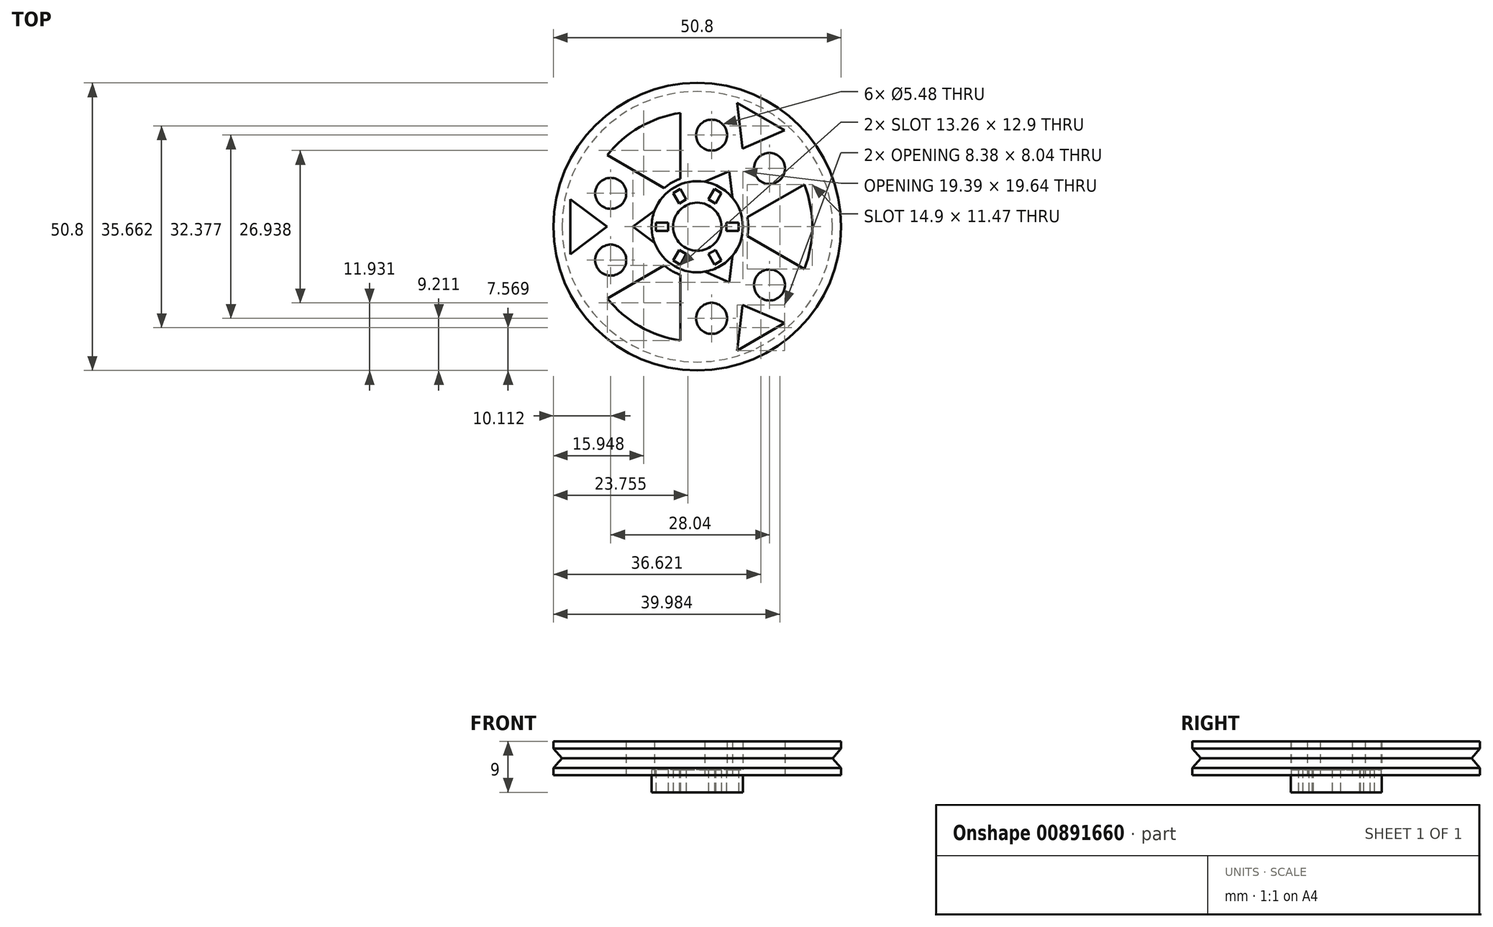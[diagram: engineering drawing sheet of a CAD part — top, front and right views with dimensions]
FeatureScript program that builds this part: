
annotation { "Feature Type Name" : "Feature", "Feature Type Description" : "" }
export const myFeature = defineFeature(function(context is Context, id is Id, definition is map)
    precondition{}
    {
        {
            var Q0;
            Q0=qCreatedBy(makeId("Top.planeOp"),FACE);
            var sketch = newSketch(context, id + "F0", { "sketchPlane" : qUnion([Q0])});
            skCircle(sketch, "E0", {"center": v(0, 0) * mm, "radius": 25.4 * mm});
            skCircle(sketch, "E1", {"center": v(0, 0) * mm, "radius": 8.05 * mm});
            skArc(sketch, "E2", {"start": v(-3, 8.49) * mm, "mid": v(-4.5, 7.8) * mm, "end": v(-5.85, 6.84) * mm});
            skArc(sketch, "E3.0", {"start": v(-3, 20.1) * mm, "mid": v(-10.16, 17.6) * mm, "end": v(-15.9, 12.65) * mm});
            skPoint(sketch, "E4.orphan", {"position": v(0, 21.15) * mm});
            skLineSegment(sketch, "E5.0", {"start": v(-3, 8.49) * mm, "end": v(-3, 20.1) * mm});
            skLineSegment(sketch, "E6.0", {"start": v(8.85, 1.64) * mm, "end": v(18.9, 7.45) * mm});
            skPoint(sketch, "E7.start.orphan", {"position": v(0, 8.05) * mm});
            skLineSegment(sketch, "E8.1.0", {"start": v(-5.85, -6.84) * mm, "end": v(-15.9, -12.65) * mm});
            skLineSegment(sketch, "E8.1.1", {"start": v(-5.85, 6.84) * mm, "end": v(-15.9, 12.65) * mm});
            skArc(sketch, "E9.trimOffspring", {"start": v(8.85, -1.64) * mm, "mid": v(9, 0) * mm, "end": v(8.85, 1.64) * mm});
            skArc(sketch, "E10.trimOffspring", {"start": v(18.9, -7.45) * mm, "mid": v(20.32, 0) * mm, "end": v(18.9, 7.45) * mm});
            skLineSegment(sketch, "E11.1.2.0", {"start": v(8.85, -1.64) * mm, "end": v(18.9, -7.45) * mm});
            skLineSegment(sketch, "E11.3.2.0", {"start": v(-3, -8.49) * mm, "end": v(-3, -20.1) * mm});
            skArc(sketch, "E12.trimOffspring", {"start": v(-15.9, -12.65) * mm, "mid": v(-10.16, -17.6) * mm, "end": v(-3, -20.1) * mm});
            skArc(sketch, "E13.trimOffspring", {"start": v(-5.85, -6.84) * mm, "mid": v(-4.5, -7.8) * mm, "end": v(-3, -8.49) * mm});
            skLineSegment(sketch, "E14", {"start": v(-22.44, 0) * mm, "end": v(-15.95, 0) * mm});
            skLineSegment(sketch, "E15", {"start": v(-15.95, 0) * mm, "end": v(-22.44, -4.84) * mm});
            skLineSegment(sketch, "E16", {"start": v(-22.44, -4.84) * mm, "end": v(-22.44, 0) * mm});
            skLineSegment(sketch, "E17.MirrorCS", {"start": v(-15.95, 0) * mm, "end": v(-22.44, 4.84) * mm});
            skLineSegment(sketch, "E18.MirrorCS", {"start": v(-22.44, 4.84) * mm, "end": v(-22.44, 0) * mm});
            skCircle(sketch, "E19", {"center": v(-15.29, -5.9) * mm, "radius": 2.74 * mm});
            skCircle(sketch, "E20.MirrorC", {"center": v(-15.29, 5.9) * mm, "radius": 2.74 * mm});
            skLineSegment(sketch, "E21", {"start": v(-13.64, -0.96) * mm, "end": v(-13.64, 1.42) * mm, "construction": true});
            skLineSegment(sketch, "E22.MirrorCS", {"start": v(-11.34, 0) * mm, "end": v(-4.84, 4.84) * mm});
            skLineSegment(sketch, "E23.MirrorCS", {"start": v(-11.34, 0) * mm, "end": v(-4.84, -4.84) * mm});
            skLineSegment(sketch, "E24.MirrorCS", {"start": v(-4.84, -4.84) * mm, "end": v(-4.84, 0) * mm});
            skLineSegment(sketch, "E25.MirrorCS", {"start": v(-4.84, 4.84) * mm, "end": v(-4.84, 0) * mm});
            skLineSegment(sketch, "E26.1.0", {"start": v(7.97, -13.8) * mm, "end": v(7.03, -21.85) * mm});
            skLineSegment(sketch, "E26.1.1", {"start": v(7.97, -13.8) * mm, "end": v(15.4, -17.02) * mm});
            skLineSegment(sketch, "E26.1.2", {"start": v(15.4, -17.02) * mm, "end": v(11.22, -19.44) * mm});
            skLineSegment(sketch, "E26.1.3", {"start": v(7.03, -21.85) * mm, "end": v(11.22, -19.44) * mm});
            skCircle(sketch, "E26.1.4", {"center": v(2.54, -16.19) * mm, "radius": 2.74 * mm});
            skCircle(sketch, "E26.1.5", {"center": v(12.75, -10.3) * mm, "radius": 2.74 * mm});
            skLineSegment(sketch, "E26.1.6", {"start": v(5.67, -9.82) * mm, "end": v(-1.77, -6.61) * mm});
            skLineSegment(sketch, "E26.1.7", {"start": v(-1.77, -6.61) * mm, "end": v(2.42, -4.2) * mm});
            skLineSegment(sketch, "E26.1.8", {"start": v(6.61, -1.78) * mm, "end": v(2.42, -4.2) * mm});
            skLineSegment(sketch, "E26.1.9", {"start": v(5.67, -9.82) * mm, "end": v(6.61, -1.78) * mm});
            skLineSegment(sketch, "E26.2.0", {"start": v(7.97, 13.8) * mm, "end": v(15.4, 17.02) * mm});
            skLineSegment(sketch, "E26.2.1", {"start": v(7.97, 13.8) * mm, "end": v(7.03, 21.85) * mm});
            skLineSegment(sketch, "E26.2.2", {"start": v(7.03, 21.85) * mm, "end": v(11.22, 19.44) * mm});
            skLineSegment(sketch, "E26.2.3", {"start": v(15.4, 17.02) * mm, "end": v(11.22, 19.44) * mm});
            skCircle(sketch, "E26.2.4", {"center": v(12.75, 10.3) * mm, "radius": 2.74 * mm});
            skCircle(sketch, "E26.2.5", {"center": v(2.54, 16.19) * mm, "radius": 2.74 * mm});
            skLineSegment(sketch, "E26.2.6", {"start": v(5.67, 9.82) * mm, "end": v(6.61, 1.78) * mm});
            skLineSegment(sketch, "E26.2.7", {"start": v(6.61, 1.78) * mm, "end": v(2.42, 4.2) * mm});
            skLineSegment(sketch, "E26.2.8", {"start": v(-1.77, 6.61) * mm, "end": v(2.42, 4.2) * mm});
            skLineSegment(sketch, "E26.2.9", {"start": v(5.67, 9.82) * mm, "end": v(-1.77, 6.61) * mm});
            skSolve(sketch);
        }
        {
            var Q0;
            Q0=makeQuery(id+"F0.imprint","IMPRINT",FACE,{"disambiguationData":[TD([[makeQuery(id+"F0.imprint","IMPRINT",EDGE,{"derivedFrom":sQuery(id+"F0.wireOp",EDGE,"E0")}),1.0]])]});
            var Q1;
            Q1=makeQuery(id+"F0.imprint","IMPRINT",FACE,{"disambiguationData":[TD([[makeQuery(id+"F0.imprint","IMPRINT",EDGE,{"derivedFrom":sQuery(id+"F0.wireOp",EDGE,"E1")}),-1.0]])]});
            extrude(context, id + "F1", {"entities" : qUnion([Q0, Q1]), "endBound" : BoundingType.SYMMETRIC, "depth" : 6 * mm, "offsetDistance" : 25.4 * mm});
        }
        {
            var Q0;
            Q0=makeQuery(id+"F1.opExtrude","CAP_FACE",FACE,{"disambiguationData":[OSD([sQuery(id+"F0.wireOp",EDGE,"E0"),sQuery(id+"F0.wireOp",EDGE,"E1"),sQuery(id+"F0.wireOp",EDGE,"E2"),sQuery(id+"F0.wireOp",EDGE,"E3.0"),sQuery(id+"F0.wireOp",EDGE,"E5.0"),sQuery(id+"F0.wireOp",EDGE,"E6.0"),sQuery(id+"F0.wireOp",EDGE,"E8.1.0"),sQuery(id+"F0.wireOp",EDGE,"E8.1.1"),sQuery(id+"F0.wireOp",EDGE,"E9.trimOffspring"),sQuery(id+"F0.wireOp",EDGE,"E10.trimOffspring"),sQuery(id+"F0.wireOp",EDGE,"E11.1.2.0"),sQuery(id+"F0.wireOp",EDGE,"E11.3.2.0"),sQuery(id+"F0.wireOp",EDGE,"E12.trimOffspring"),sQuery(id+"F0.wireOp",EDGE,"E13.trimOffspring"),sQuery(id+"F0.wireOp",EDGE,"E15"),sQuery(id+"F0.wireOp",EDGE,"E16"),sQuery(id+"F0.wireOp",EDGE,"E17.MirrorCS"),sQuery(id+"F0.wireOp",EDGE,"E18.MirrorCS"),sQuery(id+"F0.wireOp",EDGE,"E19"),sQuery(id+"F0.wireOp",EDGE,"E20.MirrorC"),sQuery(id+"F0.wireOp",EDGE,"E22.MirrorCS"),sQuery(id+"F0.wireOp",EDGE,"E23.MirrorCS"),sQuery(id+"F0.wireOp",EDGE,"E26.1.0"),sQuery(id+"F0.wireOp",EDGE,"E26.1.1"),sQuery(id+"F0.wireOp",EDGE,"E26.1.2"),sQuery(id+"F0.wireOp",EDGE,"E26.1.3"),sQuery(id+"F0.wireOp",EDGE,"E26.1.4"),sQuery(id+"F0.wireOp",EDGE,"E26.1.5"),sQuery(id+"F0.wireOp",EDGE,"E26.1.6"),sQuery(id+"F0.wireOp",EDGE,"E26.1.9"),sQuery(id+"F0.wireOp",EDGE,"E26.2.0"),sQuery(id+"F0.wireOp",EDGE,"E26.2.1"),sQuery(id+"F0.wireOp",EDGE,"E26.2.2"),sQuery(id+"F0.wireOp",EDGE,"E26.2.3"),sQuery(id+"F0.wireOp",EDGE,"E26.2.4"),sQuery(id+"F0.wireOp",EDGE,"E26.2.5"),sQuery(id+"F0.wireOp",EDGE,"E26.2.6"),sQuery(id+"F0.wireOp",EDGE,"E26.2.9")])],"isStart":true});
            var sketch = newSketch(context, id + "F2", { "sketchPlane" : qUnion([Q0])});
            skCircle(sketch, "E27", {"center": v(0, 0) * mm, "radius": 8.05 * mm});
            skCircle(sketch, "E28", {"center": v(0, 0) * mm, "radius": 4.25 * mm});
            skLineSegment(sketch, "E29.bottom", {"start": v(-5.15, 0.73) * mm, "end": v(-7.29, 0.73) * mm});
            skLineSegment(sketch, "E29.top", {"start": v(-5.15, -0.73) * mm, "end": v(-7.29, -0.73) * mm});
            skLineSegment(sketch, "E29.left", {"start": v(-5.15, 0.73) * mm, "end": v(-5.15, -0.73) * mm});
            skLineSegment(sketch, "E29.right", {"start": v(-7.29, 0.73) * mm, "end": v(-7.29, -0.73) * mm});
            skPoint(sketch, "E29.middle", {"position": v(-6.22, 0) * mm});
            skLineSegment(sketch, "E30.1.0", {"start": v(-3.2, -4.1) * mm, "end": v(-1.94, -4.83) * mm});
            skLineSegment(sketch, "E30.1.1", {"start": v(-3.2, -4.1) * mm, "end": v(-4.28, -5.95) * mm});
            skLineSegment(sketch, "E30.1.2", {"start": v(-4.28, -5.95) * mm, "end": v(-3.01, -6.68) * mm});
            skLineSegment(sketch, "E30.1.3", {"start": v(-1.94, -4.83) * mm, "end": v(-3.01, -6.68) * mm});
            skLineSegment(sketch, "E30.2.0", {"start": v(1.94, -4.83) * mm, "end": v(3.2, -4.1) * mm});
            skLineSegment(sketch, "E30.2.1", {"start": v(1.94, -4.83) * mm, "end": v(3.01, -6.68) * mm});
            skLineSegment(sketch, "E30.2.2", {"start": v(3.01, -6.68) * mm, "end": v(4.28, -5.95) * mm});
            skLineSegment(sketch, "E30.2.3", {"start": v(3.2, -4.1) * mm, "end": v(4.28, -5.95) * mm});
            skLineSegment(sketch, "E31.2.3.0", {"start": v(5.15, -0.73) * mm, "end": v(5.15, 0.73) * mm});
            skLineSegment(sketch, "E31.3.3.0", {"start": v(5.15, -0.73) * mm, "end": v(7.29, -0.73) * mm});
            skLineSegment(sketch, "E31.6.3.0", {"start": v(7.29, -0.73) * mm, "end": v(7.29, 0.73) * mm});
            skLineSegment(sketch, "E31.9.3.0", {"start": v(5.15, 0.73) * mm, "end": v(7.29, 0.73) * mm});
            skLineSegment(sketch, "E31.2.4.0", {"start": v(3.2, 4.1) * mm, "end": v(1.94, 4.83) * mm});
            skLineSegment(sketch, "E31.3.4.0", {"start": v(3.2, 4.1) * mm, "end": v(4.28, 5.95) * mm});
            skLineSegment(sketch, "E31.6.4.0", {"start": v(4.28, 5.95) * mm, "end": v(3.01, 6.68) * mm});
            skLineSegment(sketch, "E31.9.4.0", {"start": v(1.94, 4.83) * mm, "end": v(3.01, 6.68) * mm});
            skLineSegment(sketch, "E32.2.5.0", {"start": v(-1.94, 4.83) * mm, "end": v(-3.2, 4.1) * mm});
            skLineSegment(sketch, "E32.3.5.0", {"start": v(-1.94, 4.83) * mm, "end": v(-3.01, 6.68) * mm});
            skLineSegment(sketch, "E32.6.5.0", {"start": v(-3.01, 6.68) * mm, "end": v(-4.28, 5.95) * mm});
            skLineSegment(sketch, "E32.9.5.0", {"start": v(-3.2, 4.1) * mm, "end": v(-4.28, 5.95) * mm});
            skSolve(sketch);
        }
        {
            var Q0;
            Q0=makeQuery(id+"F2.imprint","IMPRINT",FACE,{"disambiguationData":[TD([[makeQuery(id+"F2.imprint","IMPRINT",EDGE,{"derivedFrom":sQuery(id+"F2.wireOp",EDGE,"E28")}),-1.0]])]});
            extrude(context, id + "F3", {"entities" : qUnion([Q0]), "operationType" : NewBodyOperationType.ADD, "oppositeDirection" : true, "depth" : 1 * mm, "offsetDistance" : 25.4 * mm});
        }
        {
            var Q0;
            Q0=qCreatedBy(makeId("Right.planeOp"),FACE);
            var sketch = newSketch(context, id + "F4", { "sketchPlane" : qUnion([Q0])});
            skLineSegment(sketch, "E33", {"start": v(25.4, 0) * mm, "end": v(23.9, 0) * mm});
            skLineSegment(sketch, "E34", {"start": v(23.9, 0) * mm, "end": v(25.42, -1.75) * mm});
            skLineSegment(sketch, "E35", {"start": v(25.42, -1.75) * mm, "end": v(25.4, 0) * mm});
            skLineSegment(sketch, "E36.MirrorCS", {"start": v(23.9, 0) * mm, "end": v(25.42, 1.75) * mm});
            skLineSegment(sketch, "E37.MirrorCS", {"start": v(25.42, 1.75) * mm, "end": v(25.4, 0) * mm});
            skLineSegment(sketch, "E38", {"start": v(0, 0) * mm, "end": v(0, 14.16) * mm, "construction": true});
            skSolve(sketch);
        }
        {
            var Q0;
            Q0 = qSketchRegion(id + "F4", true);
            var Q1;
            Q1=sQuery(id+"F4.wireOp",EDGE,"E38");
            revolve(context, id + "F5", {"operationType" : NewBodyOperationType.REMOVE, "surfaceOperationType" : NewSurfaceOperationType.NEW, "entities" : qUnion([Q0]), "axis" : qUnion([Q1]), "revolveType" : RevolveType.FULL, "oppositeDirection" : true});
        }
        {
            var Q0;
            Q0=makeQuery(id+"F3.boolean.opBoolean","MERGE",FACE,{"derivedFrom":[makeQuery(id+"F1.opExtrude","CAP_FACE",FACE,{"disambiguationData":[OSD([sQuery(id+"F0.wireOp",EDGE,"E0"),sQuery(id+"F0.wireOp",EDGE,"E1"),sQuery(id+"F0.wireOp",EDGE,"E2"),sQuery(id+"F0.wireOp",EDGE,"E3.0"),sQuery(id+"F0.wireOp",EDGE,"E5.0"),sQuery(id+"F0.wireOp",EDGE,"E6.0"),sQuery(id+"F0.wireOp",EDGE,"E8.1.0"),sQuery(id+"F0.wireOp",EDGE,"E8.1.1"),sQuery(id+"F0.wireOp",EDGE,"E9.trimOffspring"),sQuery(id+"F0.wireOp",EDGE,"E10.trimOffspring"),sQuery(id+"F0.wireOp",EDGE,"E11.1.2.0"),sQuery(id+"F0.wireOp",EDGE,"E11.3.2.0"),sQuery(id+"F0.wireOp",EDGE,"E12.trimOffspring"),sQuery(id+"F0.wireOp",EDGE,"E13.trimOffspring"),sQuery(id+"F0.wireOp",EDGE,"E15"),sQuery(id+"F0.wireOp",EDGE,"E16"),sQuery(id+"F0.wireOp",EDGE,"E17.MirrorCS"),sQuery(id+"F0.wireOp",EDGE,"E18.MirrorCS"),sQuery(id+"F0.wireOp",EDGE,"E19"),sQuery(id+"F0.wireOp",EDGE,"E20.MirrorC"),sQuery(id+"F0.wireOp",EDGE,"E22.MirrorCS"),sQuery(id+"F0.wireOp",EDGE,"E23.MirrorCS"),sQuery(id+"F0.wireOp",EDGE,"E26.1.0"),sQuery(id+"F0.wireOp",EDGE,"E26.1.1"),sQuery(id+"F0.wireOp",EDGE,"E26.1.2"),sQuery(id+"F0.wireOp",EDGE,"E26.1.3"),sQuery(id+"F0.wireOp",EDGE,"E26.1.4"),sQuery(id+"F0.wireOp",EDGE,"E26.1.5"),sQuery(id+"F0.wireOp",EDGE,"E26.1.6"),sQuery(id+"F0.wireOp",EDGE,"E26.1.9"),sQuery(id+"F0.wireOp",EDGE,"E26.2.0"),sQuery(id+"F0.wireOp",EDGE,"E26.2.1"),sQuery(id+"F0.wireOp",EDGE,"E26.2.2"),sQuery(id+"F0.wireOp",EDGE,"E26.2.3"),sQuery(id+"F0.wireOp",EDGE,"E26.2.4"),sQuery(id+"F0.wireOp",EDGE,"E26.2.5"),sQuery(id+"F0.wireOp",EDGE,"E26.2.6"),sQuery(id+"F0.wireOp",EDGE,"E26.2.9")])],"isStart":true}),makeQuery(id+"F3.opExtrude","CAP_FACE",FACE,{"disambiguationData":[OSD([sQuery(id+"F2.wireOp",EDGE,"E27"),sQuery(id+"F2.wireOp",EDGE,"E28"),sQuery(id+"F2.wireOp",EDGE,"E29.bottom"),sQuery(id+"F2.wireOp",EDGE,"E29.top"),sQuery(id+"F2.wireOp",EDGE,"E29.left"),sQuery(id+"F2.wireOp",EDGE,"E29.right"),sQuery(id+"F2.wireOp",EDGE,"E30.1.0"),sQuery(id+"F2.wireOp",EDGE,"E30.1.1"),sQuery(id+"F2.wireOp",EDGE,"E30.1.2"),sQuery(id+"F2.wireOp",EDGE,"E30.1.3"),sQuery(id+"F2.wireOp",EDGE,"E30.2.0"),sQuery(id+"F2.wireOp",EDGE,"E30.2.1"),sQuery(id+"F2.wireOp",EDGE,"E30.2.2"),sQuery(id+"F2.wireOp",EDGE,"E30.2.3"),sQuery(id+"F2.wireOp",EDGE,"E31.2.3.0"),sQuery(id+"F2.wireOp",EDGE,"E31.3.3.0"),sQuery(id+"F2.wireOp",EDGE,"E31.6.3.0"),sQuery(id+"F2.wireOp",EDGE,"E31.9.3.0"),sQuery(id+"F2.wireOp",EDGE,"E31.2.4.0"),sQuery(id+"F2.wireOp",EDGE,"E31.3.4.0"),sQuery(id+"F2.wireOp",EDGE,"E31.6.4.0"),sQuery(id+"F2.wireOp",EDGE,"E31.9.4.0"),sQuery(id+"F2.wireOp",EDGE,"E32.2.5.0"),sQuery(id+"F2.wireOp",EDGE,"E32.3.5.0"),sQuery(id+"F2.wireOp",EDGE,"E32.6.5.0"),sQuery(id+"F2.wireOp",EDGE,"E32.9.5.0")])],"isStart":true})]});
            var sketch = newSketch(context, id + "F6", { "sketchPlane" : qUnion([Q0])});
            skCircle(sketch, "E39", {"center": v(0, 0) * mm, "radius": 8.05 * mm});
            skCircle(sketch, "E40", {"center": v(0, 0) * mm, "radius": 4.25 * mm});
            skSolve(sketch);
        }
        {
            var Q0;
            Q0 = qSketchRegion(id + "F6", true);
            extrude(context, id + "F7", {"entities" : qUnion([Q0]), "operationType" : NewBodyOperationType.ADD, "depth" : 3 * mm, "offsetDistance" : 25.4 * mm});
        }
        {
            var Q0;
            Q0=makeQuery(id+"F7.boolean.opBoolean","SPLIT",FACE,{"disambiguationData":[TD([makeQuery(id+"F3.opExtrude","SWEPT_FACE",FACE,{"disambiguationData":[OSD([sQuery(id+"F2.wireOp",EDGE,"E29.bottom")])]})])],"derivedFrom":makeQuery(id+"F7.opExtrude","CAP_FACE",FACE,{"disambiguationData":[OSD([sQuery(id+"F6.wireOp",EDGE,"E39"),sQuery(id+"F6.wireOp",EDGE,"E40")])],"isStart":true})});
            var Q1;
            Q1=makeQuery(id+"F7.boolean.opBoolean","SPLIT",FACE,{"disambiguationData":[TD([makeQuery(id+"F3.opExtrude","SWEPT_FACE",FACE,{"disambiguationData":[OSD([sQuery(id+"F2.wireOp",EDGE,"E30.1.0")])]})])],"derivedFrom":makeQuery(id+"F7.opExtrude","CAP_FACE",FACE,{"disambiguationData":[OSD([sQuery(id+"F6.wireOp",EDGE,"E39"),sQuery(id+"F6.wireOp",EDGE,"E40")])],"isStart":true})});
            var Q2;
            Q2=makeQuery(id+"F7.boolean.opBoolean","SPLIT",FACE,{"disambiguationData":[TD([makeQuery(id+"F3.opExtrude","SWEPT_FACE",FACE,{"disambiguationData":[OSD([sQuery(id+"F2.wireOp",EDGE,"E30.2.0")])]})])],"derivedFrom":makeQuery(id+"F7.opExtrude","CAP_FACE",FACE,{"disambiguationData":[OSD([sQuery(id+"F6.wireOp",EDGE,"E39"),sQuery(id+"F6.wireOp",EDGE,"E40")])],"isStart":true})});
            var Q3;
            Q3=makeQuery(id+"F7.boolean.opBoolean","SPLIT",FACE,{"disambiguationData":[TD([makeQuery(id+"F3.opExtrude","SWEPT_FACE",FACE,{"disambiguationData":[OSD([sQuery(id+"F2.wireOp",EDGE,"E31.2.3.0")])]})])],"derivedFrom":makeQuery(id+"F7.opExtrude","CAP_FACE",FACE,{"disambiguationData":[OSD([sQuery(id+"F6.wireOp",EDGE,"E39"),sQuery(id+"F6.wireOp",EDGE,"E40")])],"isStart":true})});
            var Q4;
            Q4=makeQuery(id+"F7.boolean.opBoolean","SPLIT",FACE,{"disambiguationData":[TD([makeQuery(id+"F3.opExtrude","SWEPT_FACE",FACE,{"disambiguationData":[OSD([sQuery(id+"F2.wireOp",EDGE,"E31.2.4.0")])]})])],"derivedFrom":makeQuery(id+"F7.opExtrude","CAP_FACE",FACE,{"disambiguationData":[OSD([sQuery(id+"F6.wireOp",EDGE,"E39"),sQuery(id+"F6.wireOp",EDGE,"E40")])],"isStart":true})});
            var Q5;
            Q5=makeQuery(id+"F7.boolean.opBoolean","SPLIT",FACE,{"disambiguationData":[TD([makeQuery(id+"F3.opExtrude","SWEPT_FACE",FACE,{"disambiguationData":[OSD([sQuery(id+"F2.wireOp",EDGE,"E32.2.5.0")])]})])],"derivedFrom":makeQuery(id+"F7.opExtrude","CAP_FACE",FACE,{"disambiguationData":[OSD([sQuery(id+"F6.wireOp",EDGE,"E39"),sQuery(id+"F6.wireOp",EDGE,"E40")])],"isStart":true})});
            extrude(context, id + "F8", {"entities" : qUnion([Q0, Q1, Q2, Q3, Q4, Q5]), "operationType" : NewBodyOperationType.REMOVE, "endBound" : BoundingType.THROUGH_ALL, "oppositeDirection" : true, "depth" : 25.4 * mm, "offsetDistance" : 25.4 * mm});
        }
    });
